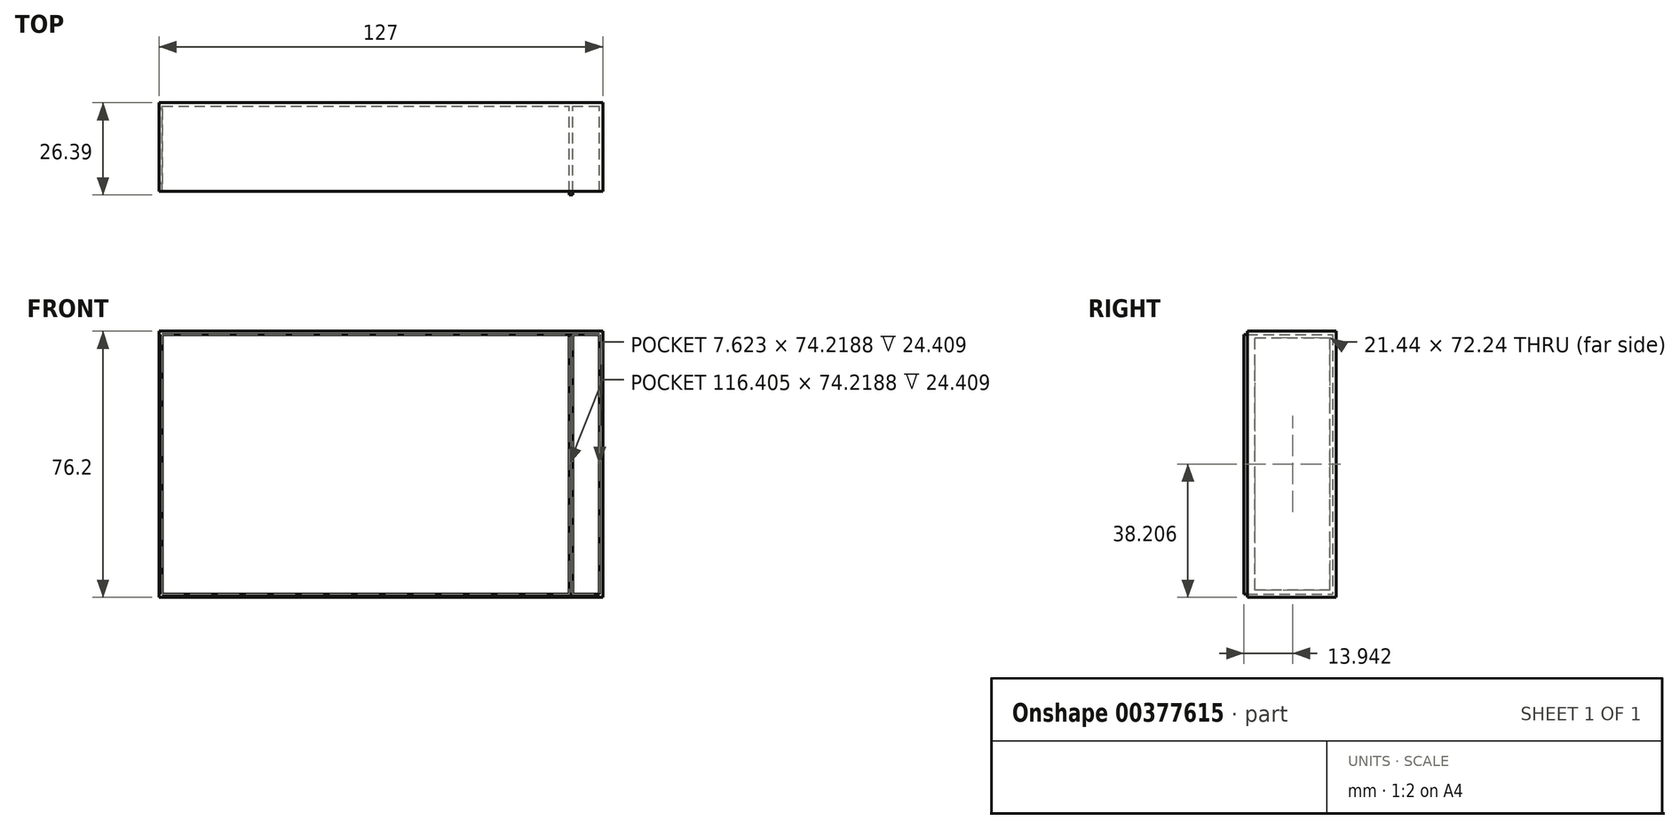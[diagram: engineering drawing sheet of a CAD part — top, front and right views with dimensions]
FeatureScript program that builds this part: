
annotation { "Feature Type Name" : "Feature", "Feature Type Description" : "" }
export const myFeature = defineFeature(function(context is Context, id is Id, definition is map)
    precondition{}
    {
        {
            var Q0;
            Q0=qCreatedBy(makeId("Front.planeOp"),FACE);
            var sketch = newSketch(context, id + "F0", { "sketchPlane" : qUnion([Q0])});
            skLineSegment(sketch, "E0.bottom", {"start": v(-63.5, 38.1) * mm, "end": v(63.5, 38.1) * mm});
            skLineSegment(sketch, "E0.top", {"start": v(-63.5, -38.1) * mm, "end": v(63.5, -38.1) * mm});
            skLineSegment(sketch, "E0.left", {"start": v(-63.5, 38.1) * mm, "end": v(-63.5, -38.1) * mm});
            skLineSegment(sketch, "E0.right", {"start": v(63.5, 38.1) * mm, "end": v(63.5, -38.1) * mm});
            skPoint(sketch, "E0.middle", {"position": v(0, 0) * mm});
            skSolve(sketch);
        }
        {
            var Q0;
            Q0 = qSketchRegion(id + "F0", true);
            extrude(context, id + "F1", {"entities" : qUnion([Q0]), "depth" : 25.4 * mm});
        }
        {
            var Q0;
            Q0=makeQuery(id+"F1.opExtrude","CAP_FACE",FACE,{"disambiguationData":[OSD([sQuery(id+"F0.wireOp",EDGE,"E0.bottom"),sQuery(id+"F0.wireOp",EDGE,"E0.top"),sQuery(id+"F0.wireOp",EDGE,"E0.left"),sQuery(id+"F0.wireOp",EDGE,"E0.right")])],"isStart":false});
            shell(context, id + "F2", {"entities" : qUnion([Q0]), "thickness" : 1 * mm});
        }
        {
            var Q0;
            Q0=makeQuery(id+"F2.opShell","OFFSET_FACE",FACE,{"disambiguationData":[OSD([sQuery(id+"F0.wireOp",EDGE,"E0.bottom"),sQuery(id+"F0.wireOp",EDGE,"E0.top"),sQuery(id+"F0.wireOp",EDGE,"E0.left"),sQuery(id+"F0.wireOp",EDGE,"E0.right")])]});
            var sketch = newSketch(context, id + "F3", { "sketchPlane" : qUnion([Q0])});
            skLineSegment(sketch, "E1", {"start": v(54.89, 37.1) * mm, "end": v(54.89, -37.1) * mm});
            skLineSegment(sketch, "E2", {"start": v(54.89, 37.1) * mm, "end": v(53.9, 37.1) * mm});
            skLineSegment(sketch, "E3", {"start": v(53.9, 37.1) * mm, "end": v(53.9, -37.1) * mm});
            skLineSegment(sketch, "E4", {"start": v(53.9, -37.1) * mm, "end": v(54.89, -37.1) * mm});
            skSolve(sketch);
        }
        {
            var Q0;
            Q0=makeQuery(id+"F3.imprint","IMPRINT",FACE,{"disambiguationData":[TD([[makeQuery(id+"F3.imprint","IMPRINT",EDGE,{"derivedFrom":sQuery(id+"F3.wireOp",EDGE,"E1")}),-1.0]])]});
            extrude(context, id + "F4", {"entities" : qUnion([Q0]), "operationType" : NewBodyOperationType.ADD, "depth" : 25.4 * mm});
        }
        {
            var Q0;
            Q0=makeQuery(id+"F1.opExtrude","SWEPT_FACE",FACE,{"disambiguationData":[OSD([sQuery(id+"F0.wireOp",EDGE,"E0.left")])]});
            var sketch = newSketch(context, id + "F5", { "sketchPlane" : qUnion([Q0])});
            skLineSegment(sketch, "E5", {"start": v(23.17, 36.23) * mm, "end": v(1.73, 36.23) * mm});
            skLineSegment(sketch, "E6", {"start": v(1.73, -36.01) * mm, "end": v(1.73, 36.23) * mm});
            skLineSegment(sketch, "E7", {"start": v(1.73, -36.01) * mm, "end": v(23.17, -36.01) * mm});
            skLineSegment(sketch, "E8", {"start": v(23.17, -36.01) * mm, "end": v(23.17, 36.23) * mm});
            skSolve(sketch);
        }
        {
            var Q0;
            Q0=makeQuery(id+"F5.imprint","IMPRINT",FACE,{"disambiguationData":[TD([[makeQuery(id+"F5.imprint","IMPRINT",EDGE,{"derivedFrom":sQuery(id+"F5.wireOp",EDGE,"E5")}),1.0]])]});
            extrude(context, id + "F6", {"entities" : qUnion([Q0]), "operationType" : NewBodyOperationType.REMOVE, "oppositeDirection" : true, "depth" : 25.4 * mm});
        }
    });
